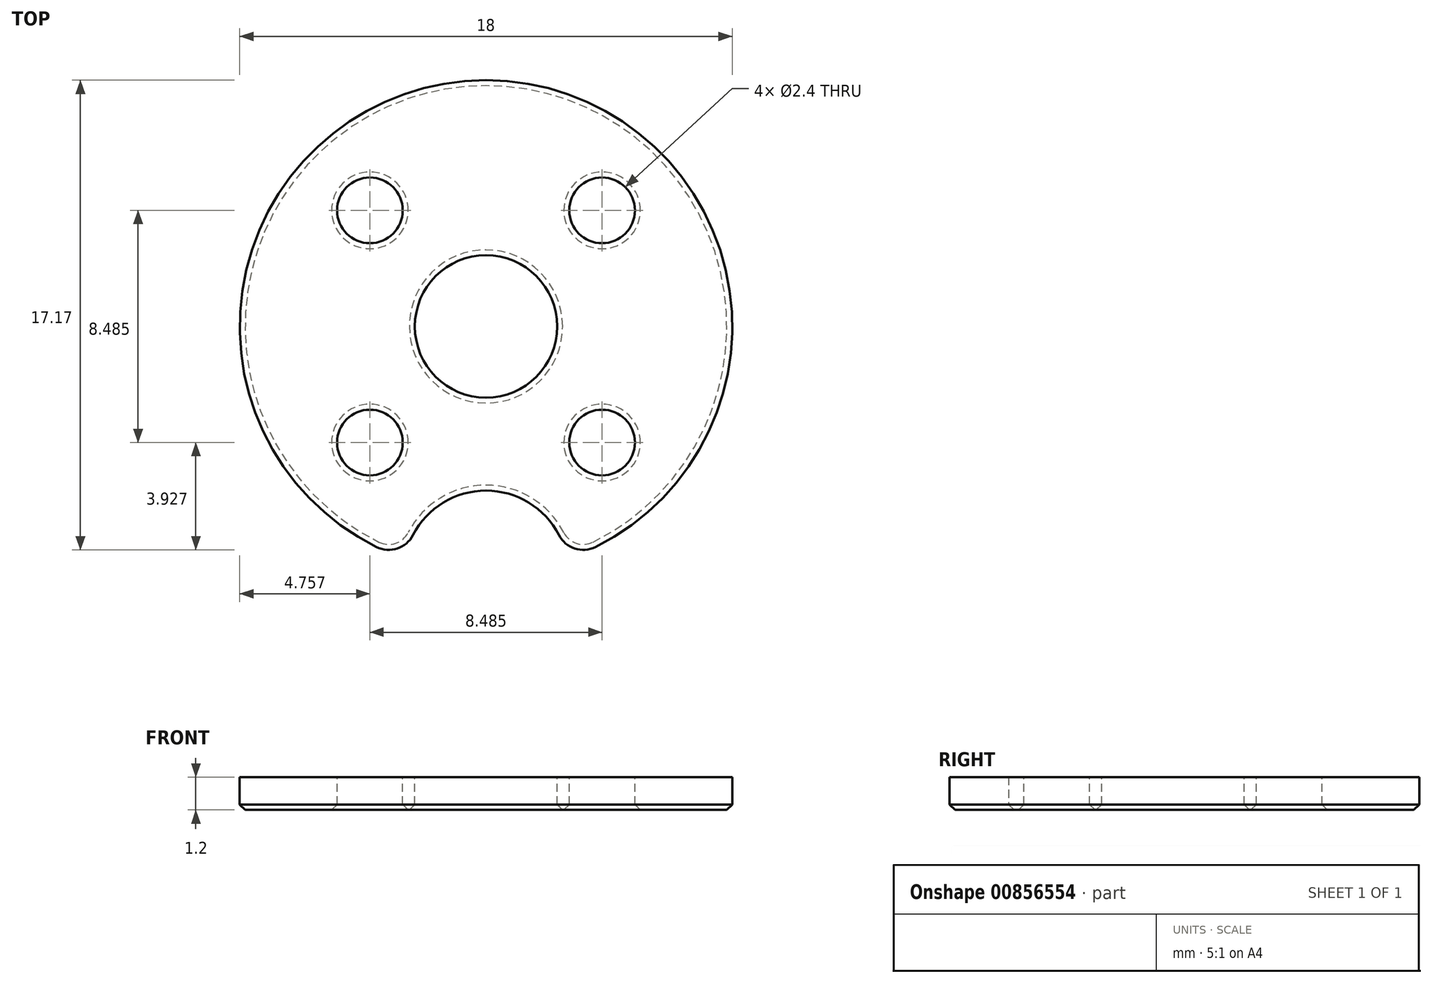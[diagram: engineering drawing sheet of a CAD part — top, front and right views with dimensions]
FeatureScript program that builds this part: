
annotation { "Feature Type Name" : "Feature", "Feature Type Description" : "" }
export const myFeature = defineFeature(function(context is Context, id is Id, definition is map)
    precondition{}
    {
        {
            var Q0;
            Q0=qCreatedBy(makeId("Top.planeOp"),FACE);
            var sketch = newSketch(context, id + "F0", { "sketchPlane" : qUnion([Q0])});
            skCircle(sketch, "E0", {"center": v(0, 0) * mm, "radius": 6 * mm, "construction": true});
            skLineSegment(sketch, "E1.bottom", {"start": v(4.24, 4.24) * mm, "end": v(-4.24, 4.24) * mm, "construction": true});
            skLineSegment(sketch, "E1.top", {"start": v(4.24, -4.24) * mm, "end": v(-4.24, -4.24) * mm, "construction": true});
            skLineSegment(sketch, "E1.left", {"start": v(4.24, 4.24) * mm, "end": v(4.24, -4.24) * mm, "construction": true});
            skLineSegment(sketch, "E1.right", {"start": v(-4.24, 4.24) * mm, "end": v(-4.24, -4.24) * mm, "construction": true});
            skCircle(sketch, "E2", {"center": v(0, 0) * mm, "radius": 2.5 * mm, "construction": true});
            skCircle(sketch, "E3", {"center": v(4.24, 4.24) * mm, "radius": 1 * mm, "construction": true});
            skCircle(sketch, "E4.0", {"center": v(0, 0) * mm, "radius": 2.6 * mm});
            skCircle(sketch, "E5.0", {"center": v(4.24, 4.24) * mm, "radius": 1.2 * mm});
            skCircle(sketch, "E6", {"center": v(0, 0) * mm, "radius": 9 * mm});
            skCircle(sketch, "E7.1.0", {"center": v(-4.24, 4.24) * mm, "radius": 1.2 * mm});
            skCircle(sketch, "E7.2.0", {"center": v(-4.24, -4.24) * mm, "radius": 1.2 * mm});
            skCircle(sketch, "E7.3.0", {"center": v(4.24, -4.24) * mm, "radius": 1.2 * mm});
            skSolve(sketch);
        }
        {
            var Q0;
            Q0=qCreatedBy(makeId("Front.planeOp"),FACE);
            var sketch = newSketch(context, id + "F1", { "sketchPlane" : qUnion([Q0])});
            skLineSegment(sketch, "E8", {"start": v(0, 0) * mm, "end": v(0, 1.2) * mm});
            skSolve(sketch);
        }
        {
            var Q0;
            Q0=qCreatedBy(makeId("Top.planeOp"),FACE);
            var sketch = newSketch(context, id + "F2", { "sketchPlane" : qUnion([Q0])});
            skCircle(sketch, "E9.0", {"center": v(0, 0) * mm, "radius": 9 * mm, "construction": true});
            skCircle(sketch, "E10", {"center": v(0, -9) * mm, "radius": 3 * mm});
            skSolve(sketch);
        }
        {
            var Q0;
            Q0 = qSketchRegion(id + "F0", true);
            var Q1;
            Q1=sQuery(id+"F1.wireOp",EDGE,"E8");
            sweep(context, id + "F3", {"profiles" : qUnion([Q0]), "path" : qUnion([Q1])});
        }
        {
            var Q0;
            Q0 = qSketchRegion(id + "F2", true);
            extrude(context, id + "F4", {"entities" : qUnion([Q0]), "operationType" : NewBodyOperationType.REMOVE, "endBound" : BoundingType.THROUGH_ALL, "depth" : 25 * mm, "offsetDistance" : 25 * mm});
        }
        {
            var Q0;
            Q0=makeQuery(id+"F4.boolean.opBoolean","INTERSECT",EDGE,{"disambiguationData":[OD(1.0)],"derivedFrom":[makeQuery(id+"F3.opSweep","SWEPT_FACE",FACE,{"disambiguationData":[OSD([sQuery(id+"F0.wireOp",EDGE,"E6"),sQuery(id+"F1.wireOp",EDGE,"E8")])]}),makeQuery(id+"F4.opExtrude","SWEPT_FACE",FACE,{"disambiguationData":[OSD([sQuery(id+"F2.wireOp",EDGE,"E10")])]})]});
            var Q1;
            Q1=makeQuery(id+"F4.boolean.opBoolean","INTERSECT",EDGE,{"disambiguationData":[OD(0.0)],"derivedFrom":[makeQuery(id+"F3.opSweep","SWEPT_FACE",FACE,{"disambiguationData":[OSD([sQuery(id+"F0.wireOp",EDGE,"E6"),sQuery(id+"F1.wireOp",EDGE,"E8")])]}),makeQuery(id+"F4.opExtrude","SWEPT_FACE",FACE,{"disambiguationData":[OSD([sQuery(id+"F2.wireOp",EDGE,"E10")])]})]});
            fillet(context, id + "F5", {"entities" : qUnion([Q0, Q1]), "radius" : 1 * mm, "tangentPropagation" : true, "allowEdgeOverflow" : false});
        }
        {
            var Q0;
            Q0=makeQuery(id+"F3.opSweep","CAP_FACE",FACE,{"disambiguationData":[OSD([sQuery(id+"F0.wireOp",EDGE,"E4.0"),sQuery(id+"F0.wireOp",EDGE,"E5.0"),sQuery(id+"F0.wireOp",EDGE,"E6"),sQuery(id+"F0.wireOp",EDGE,"E7.1.0"),sQuery(id+"F0.wireOp",EDGE,"E7.2.0"),sQuery(id+"F0.wireOp",EDGE,"E7.3.0"),sQuery(id+"F1.wireOp",VERTEX,"E8.start")])],"isStart":true});
            chamfer(context, id + "F6", {"entities" : qUnion([Q0]), "width" : 0.2 * mm});
        }
    });
